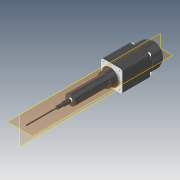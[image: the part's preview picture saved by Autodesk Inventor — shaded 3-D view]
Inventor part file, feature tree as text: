
AUTODESK INVENTOR PART (.ipt)
format: ipt  version: 2022 (Build 260153000, 153)  size: 342,016 bytes
history: native  units: in
note: dims shown in document units (in); Inventor stores cm internally (conversion verified against a paired STEP export)
features: extrude x3, sketch x3, plane x2, other x2
ambient origin geometry x8: Origin, YZ Plane, XZ Plane, XY Plane, X Axis, Y Axis, Z Axis, Center Point
bodies: Solid2 (feature_tree), Solid3 (feature_tree), Solid4 (feature_tree), Solid1 (feature_tree)
feature tree (10):
  extrude  "Extrusion2"  Depth=0.2756in TaperAngle=0.0deg
  extrude  "Extrusion3"  Depth=1.2598in TaperAngle=0.0deg
  extrude  "Extrusion4"  Depth=1.6535in TaperAngle=0.0deg
  plane  "Arbeitsebene1"
  plane  "Arbeitsebene2"
  sketch  "Skizze2"  dims[d3=0.5043in d4=0.2756in d5=0.0in]
  sketch  "Skizze3"  dims[d6=0.3937in d7=1.2598in d8=0.0in]
  sketch  "Skizze4"  dims[d9=0.0394in d10=1.6535in d11=0.0in]
  other  "Solid2:1"
  other  "Solid3:1"
